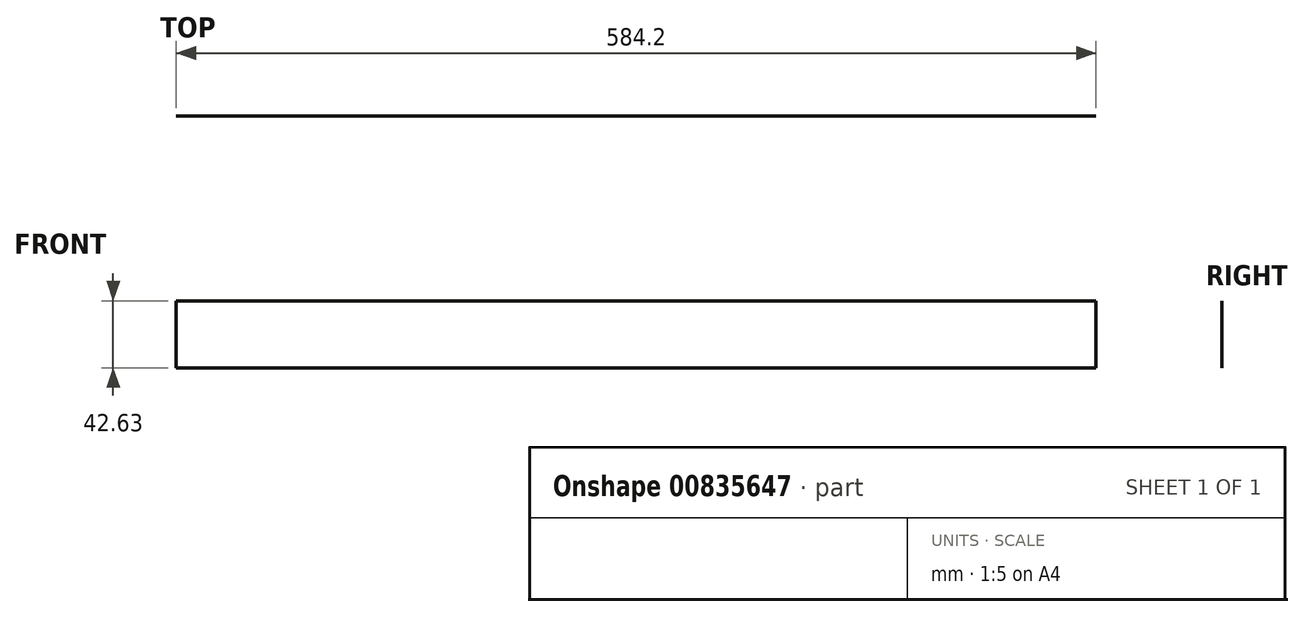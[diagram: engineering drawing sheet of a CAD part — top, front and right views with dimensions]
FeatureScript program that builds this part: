
annotation { "Feature Type Name" : "Feature", "Feature Type Description" : "" }
export const myFeature = defineFeature(function(context is Context, id is Id, definition is map)
    precondition{}
    {
        {
            var Q0;
            Q0=qCreatedBy(makeId("Front.planeOp"),FACE);
            var sketch = newSketch(context, id + "F0", { "sketchPlane" : qUnion([Q0])});
            skLineSegment(sketch, "E0.bottom", {"start": v(0, 0) * mm, "end": v(584.2, 0) * mm});
            skLineSegment(sketch, "E0.top", {"start": v(0, 42.63) * mm, "end": v(584.2, 42.63) * mm});
            skLineSegment(sketch, "E0.left", {"start": v(0, 0) * mm, "end": v(0, 42.63) * mm});
            skLineSegment(sketch, "E0.right", {"start": v(584.2, 0) * mm, "end": v(584.2, 42.63) * mm});
            skSolve(sketch);
        }
        {
            var Q0;
            Q0=makeQuery(id+"F0.imprint","IMPRINT",FACE,{"disambiguationData":[TD([[makeQuery(id+"F0.imprint","IMPRINT",EDGE,{"derivedFrom":sQuery(id+"F0.wireOp",EDGE,"E0.bottom")}),1.0]])]});
            extrude(context, id + "F1", {"entities" : qUnion([Q0]), "depth" : 1 / 254 * mm, "offsetDistance" : 25.4 * mm});
        }
    });
